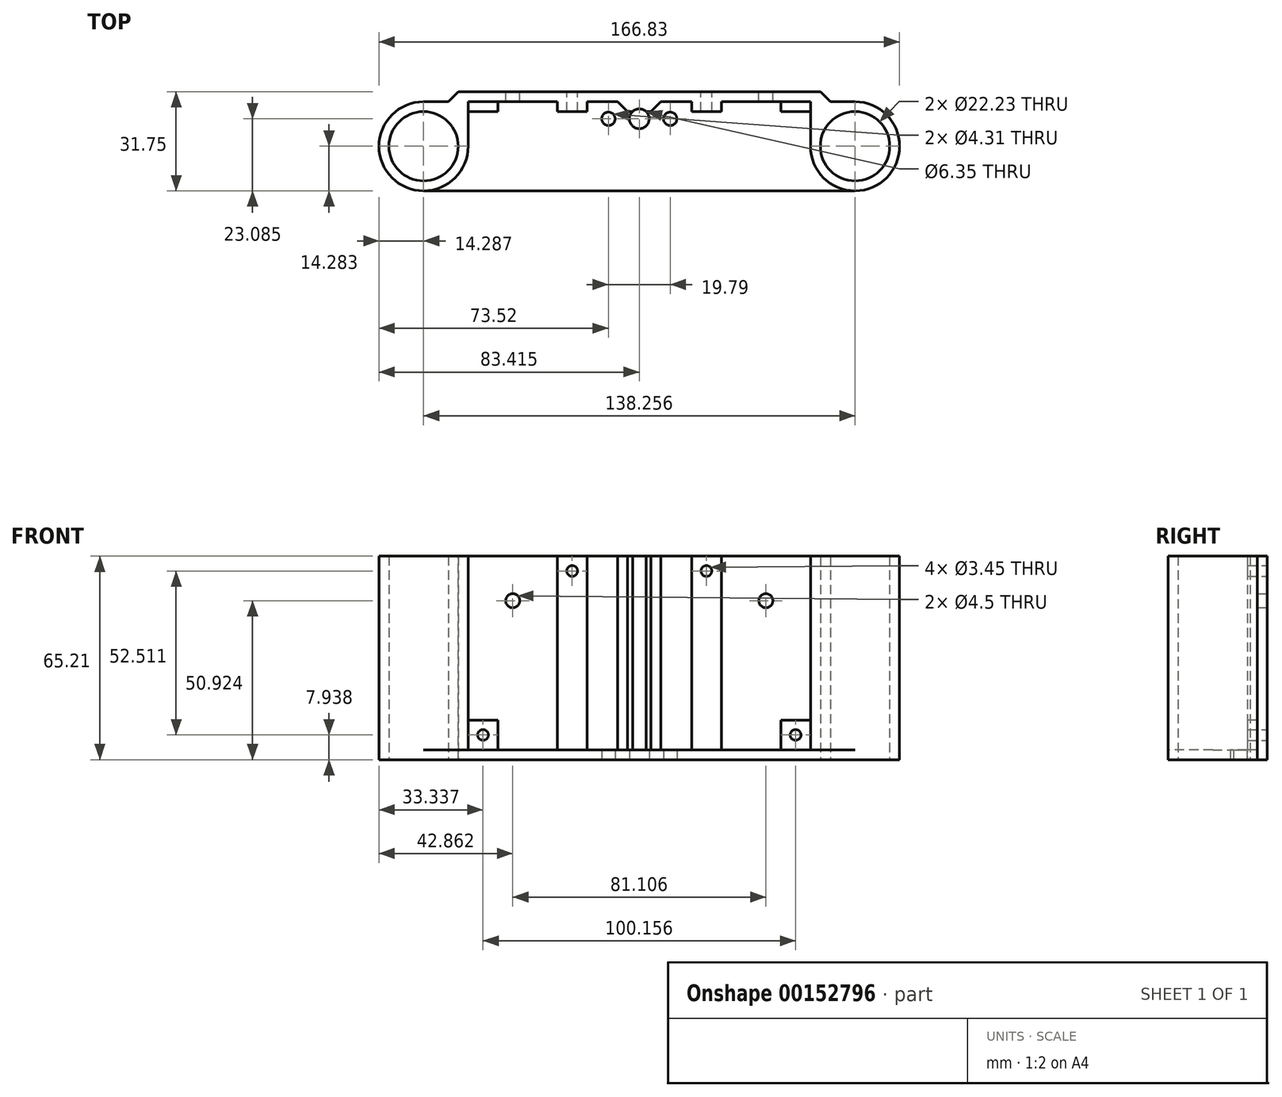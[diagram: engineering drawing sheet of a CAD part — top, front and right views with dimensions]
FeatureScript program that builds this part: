
annotation { "Feature Type Name" : "Feature", "Feature Type Description" : "" }
export const myFeature = defineFeature(function(context is Context, id is Id, definition is map)
    precondition{}
    {
        {
            var Q0;
            Q0=qCreatedBy(makeId("Top.planeOp"),FACE);
            var sketch = newSketch(context, id + "F0", { "sketchPlane" : qUnion([Q0])});
            skLineSegment(sketch, "E0.bottom", {"start": v(0, 0) * mm, "end": v(22.22, 0) * mm});
            skLineSegment(sketch, "E1.top", {"start": v(0, -14.29) * mm, "end": v(28.58, -14.29) * mm, "construction": true});
            skLineSegment(sketch, "E1.left", {"start": v(0, 0) * mm, "end": v(0, -14.29) * mm});
            skLineSegment(sketch, "E1.right", {"start": v(28.58, -3.18) * mm, "end": v(28.58, -14.29) * mm});
            skArc(sketch, "E2", {"start": v(0, -14.29) * mm, "mid": v(14.29, -28.57) * mm, "end": v(28.58, -14.29) * mm});
            skLineSegment(sketch, "E3", {"start": v(28.58, -3.18) * mm, "end": v(138.26, -3.18) * mm});
            skLineSegment(sketch, "E4.top", {"start": v(138.26, -14.29) * mm, "end": v(166.83, -14.29) * mm, "construction": true});
            skLineSegment(sketch, "E4.left", {"start": v(138.26, -3.18) * mm, "end": v(138.26, -14.29) * mm});
            skLineSegment(sketch, "E4.right", {"start": v(166.83, 0) * mm, "end": v(166.83, -14.29) * mm});
            skArc(sketch, "E5", {"start": v(138.26, -14.29) * mm, "mid": v(152.54, -28.57) * mm, "end": v(166.83, -14.29) * mm});
            skCircle(sketch, "E6", {"center": v(14.29, -14.29) * mm, "radius": 11.11 * mm});
            skCircle(sketch, "E7", {"center": v(152.54, -14.29) * mm, "radius": 11.11 * mm});
            skLineSegment(sketch, "E8", {"start": v(22.23, 0) * mm, "end": v(22.23, 3.18) * mm});
            skLineSegment(sketch, "E9", {"start": v(22.22, 3.17) * mm, "end": v(144.6, 3.17) * mm});
            skLineSegment(sketch, "E10", {"start": v(144.6, 3.18) * mm, "end": v(144.6, 0) * mm});
            skLineSegment(sketch, "E11", {"start": v(144.6, 0) * mm, "end": v(166.83, 0) * mm});
            skSolve(sketch);
        }
        {
            var Q0;
            Q0=qSketchRegion(id+"F0",true);
            extrude(context, id + "F1", {"entities" : qUnion([Q0]), "depth" : 65.2 * mm});
        }
        {
            var Q0;
            Q0=makeQuery(id+"F1.opExtrude","CAP_FACE",FACE,{"disambiguationData":[OSD([sQuery(id+"F0.wireOp",EDGE,"E0.bottom"),sQuery(id+"F0.wireOp",EDGE,"E0.top"),sQuery(id+"F0.wireOp",EDGE,"E0.left"),sQuery(id+"F0.wireOp",EDGE,"E1.left"),sQuery(id+"F0.wireOp",EDGE,"E1.right"),sQuery(id+"F0.wireOp",EDGE,"E2"),sQuery(id+"F0.wireOp",EDGE,"E3"),sQuery(id+"F0.wireOp",EDGE,"E4.left"),sQuery(id+"F0.wireOp",EDGE,"E4.right"),sQuery(id+"F0.wireOp",EDGE,"E5"),sQuery(id+"F0.wireOp",EDGE,"SdDxLh9R-VBPd-SPTP-oL8X-EhF4jRjkJOkv.bottom"),sQuery(id+"F0.wireOp",EDGE,"SdDxLh9R-VBPd-SPTP-oL8X-EhF4jRjkJOkv.right"),sQuery(id+"F0.wireOp",EDGE,"E6"),sQuery(id+"F0.wireOp",EDGE,"E7")])],"isStart":true});
            var sketch = newSketch(context, id + "F2", { "sketchPlane" : qUnion([Q0])});
            skLineSegment(sketch, "E12", {"start": v(14.29, 28.58) * mm, "end": v(152.54, 28.58) * mm});
            skLineSegment(sketch, "E13.top", {"start": v(28.58, 3.18) * mm, "end": v(138.26, 3.18) * mm});
            skLineSegment(sketch, "E13.left", {"start": v(28.58, 14.29) * mm, "end": v(28.58, 3.18) * mm});
            skLineSegment(sketch, "E13.right", {"start": v(138.26, 14.29) * mm, "end": v(138.26, 3.18) * mm});
            skArc(sketch, "E14", {"start": v(152.54, 28.57) * mm, "mid": v(142.44, 24.4) * mm, "end": v(138.26, 14.29) * mm});
            skArc(sketch, "E15", {"start": v(28.58, 14.29) * mm, "mid": v(24.4, 24.4) * mm, "end": v(14.29, 28.57) * mm});
            skSolve(sketch);
        }
        {
            var Q0;
            Q0=makeQuery(id+"F2.imprint","IMPRINT",FACE,{"disambiguationData":[TD([[makeQuery(id+"F2.imprint","IMPRINT",EDGE,{"derivedFrom":sQuery(id+"F2.wireOp",EDGE,"E12")}),-1.0]])]});
            var Q1;
            {var subQ0=sQuery(id+"F2.wireOp",EDGE,"YKqQdaZC-LU7M-u9Vu-8tjr-K4hHchLtnBJy");var subQ1=sQuery(id+"F2.wireOp",EDGE,"E13.top");var subQ2=makeQuery(id+"F2.imprint","INTERSECT",VERTEX,{"disambiguationData":[OD(0.0)],"derivedFrom":[subQ1,subQ0]});Q1=makeQuery(id+"F2.imprint","IMPRINT",FACE,{"disambiguationData":[TD([[makeQuery(id+"F2.imprint","IMPRINT",EDGE,{"disambiguationData":[TD([[subQ2,-1.0]])],"derivedFrom":subQ1}),-1.0]])]});}
            var Q2;
            Q2=makeQuery(id+"FjmdNtaRYLObFBn_1.boolean.opBoolean","COPY",FACE,{"derivedFrom":makeQuery(id+"FjmdNtaRYLObFBn_1.opExtrude","CAP_FACE",FACE,{"disambiguationData":[OSD([sQuery(id+"FSosjeWW6qpsHIW_1.wireOp",EDGE,"e9cDil25-53kW-lShf-zMKn-JTNJqIeN1P7c")])],"isStart":false})});
            extrude(context, id + "F3", {"entities" : qUnion([Q0, Q1]), "operationType" : NewBodyOperationType.ADD, "oppositeDirection" : true, "endBoundEntityFace" : qUnion([Q2]), "depth" : 3.17 * mm});
        }
        {
            var Q0;
            Q0=makeQuery(id+"F1.opExtrude","SWEPT_EDGE",EDGE,{"disambiguationData":[OSD([sQuery(id+"F0.wireOp",EDGE,"E0.bottom"),sQuery(id+"F0.wireOp",EDGE,"E1.left")])]});
            var Q1;
            Q1=makeQuery(id+"F1.opExtrude","SWEPT_EDGE",EDGE,{"disambiguationData":[OSD([sQuery(id+"F0.wireOp",EDGE,"E4.right"),sQuery(id+"F0.wireOp",EDGE,"E11")])]});
            var Q2;
            Q2=makeQuery(id+"F1.opExtrude","SWEPT_EDGE",EDGE,{"disambiguationData":[OSD([sQuery(id+"F0.wireOp",EDGE,"E0.bottom"),sQuery(id+"F0.wireOp",EDGE,"E1.left")])]});
            fillet(context, id + "F4", {"entities" : qUnion([Q0, Q1, Q2]), "radius" : 14.29 * mm, "tangentPropagation" : true, "allowEdgeOverflow" : false});
        }
        {
            var Q0;
            Q0=makeQuery(id+"F1.opExtrude","SWEPT_FACE",FACE,{"disambiguationData":[OSD([sQuery(id+"F0.wireOp",EDGE,"E9")])]});
            var sketch = newSketch(context, id + "F5", { "sketchPlane" : qUnion([Q0])});
            skLineSegment(sketch, "E16.bottom", {"start": v(-138.26, 65.21) * mm, "end": v(-123.97, 65.21) * mm, "construction": true});
            skLineSegment(sketch, "E16.top", {"start": v(-138.26, 50.92) * mm, "end": v(-123.97, 50.92) * mm, "construction": true});
            skLineSegment(sketch, "E16.left", {"start": v(-138.26, 65.21) * mm, "end": v(-138.26, 50.92) * mm, "construction": true});
            skLineSegment(sketch, "E16.right", {"start": v(-123.97, 65.21) * mm, "end": v(-123.97, 50.92) * mm, "construction": true});
            skLineSegment(sketch, "E17.bottom", {"start": v(-28.58, 65.21) * mm, "end": v(-42.86, 65.21) * mm, "construction": true});
            skLineSegment(sketch, "E17.top", {"start": v(-28.57, 50.92) * mm, "end": v(-42.86, 50.92) * mm, "construction": true});
            skLineSegment(sketch, "E17.left", {"start": v(-28.57, 65.21) * mm, "end": v(-28.57, 50.92) * mm, "construction": true});
            skLineSegment(sketch, "E17.right", {"start": v(-42.86, 65.21) * mm, "end": v(-42.86, 50.92) * mm, "construction": true});
            skLineSegment(sketch, "E18", {"start": v(-123.97, 60.45) * mm, "end": v(-104.92, 60.45) * mm, "construction": true});
            skLineSegment(sketch, "E19", {"start": v(-104.92, 60.45) * mm, "end": v(-61.91, 60.45) * mm, "construction": true});
            skLineSegment(sketch, "E20", {"start": v(-61.91, 60.45) * mm, "end": v(-42.86, 60.45) * mm, "construction": true});
            skLineSegment(sketch, "E21", {"start": v(-83.42, 60.45) * mm, "end": v(-83.42, 65.21) * mm, "construction": true});
            skLineSegment(sketch, "E22", {"start": v(-133.5, 3.17) * mm, "end": v(-133.5, 7.94) * mm, "construction": true});
            skLineSegment(sketch, "E23", {"start": v(-33.34, 3.17) * mm, "end": v(-33.34, 7.94) * mm, "construction": true});
            skCircle(sketch, "E24", {"center": v(-123.97, 50.92) * mm, "radius": 2.25 * mm});
            skCircle(sketch, "E25", {"center": v(-104.92, 60.45) * mm, "radius": 1.73 * mm});
            skCircle(sketch, "E26", {"center": v(-61.91, 60.45) * mm, "radius": 1.73 * mm});
            skCircle(sketch, "E27", {"center": v(-42.86, 50.92) * mm, "radius": 2.25 * mm});
            skCircle(sketch, "E28", {"center": v(-133.5, 7.94) * mm, "radius": 1.73 * mm});
            skCircle(sketch, "E29", {"center": v(-33.34, 7.94) * mm, "radius": 1.73 * mm});
            skLineSegment(sketch, "E30", {"start": v(-133.5, 7.94) * mm, "end": v(-138.26, 7.94) * mm, "construction": true});
            skLineSegment(sketch, "E31", {"start": v(-33.34, 7.94) * mm, "end": v(-28.58, 7.94) * mm, "construction": true});
            skSolve(sketch);
        }
        {
            var Q0;
            Q0 = qSketchRegion(id + "F5", true);
            var Q1;
            Q1=makeQuery(id+"F1.opExtrude","SWEPT_FACE",FACE,{"disambiguationData":[OSD([sQuery(id+"F0.wireOp",EDGE,"E3")])]});
            extrude(context, id + "F6", {"entities" : qUnion([Q0]), "operationType" : NewBodyOperationType.REMOVE, "endBound" : BoundingType.UP_TO_SURFACE, "oppositeDirection" : true, "endBoundEntityFace" : qUnion([Q1]), "depth" : 25.4 * mm});
        }
        {
            var Q0;
            {var subQ0=sQuery(id+"F0.wireOp",EDGE,"E11");var subQ1=sQuery(id+"F0.wireOp",EDGE,"E10");var subQ2=sQuery(id+"F0.wireOp",EDGE,"E9");var subQ3=sQuery(id+"F0.wireOp",EDGE,"E8");var subQ4=sQuery(id+"F0.wireOp",EDGE,"E7");var subQ5=sQuery(id+"F0.wireOp",EDGE,"E6");var subQ6=sQuery(id+"F0.wireOp",EDGE,"E5");var subQ7=sQuery(id+"F0.wireOp",EDGE,"E4.right");var subQ8=sQuery(id+"F0.wireOp",EDGE,"E2");var subQ9=sQuery(id+"F0.wireOp",EDGE,"E1.left");var subQ10=sQuery(id+"F0.wireOp",EDGE,"E0.bottom");Q0=makeQuery(id+"F3.boolean.opBoolean","MERGE",FACE,{"derivedFrom":[makeQuery(id+"F1.opExtrude","CAP_FACE",FACE,{"disambiguationData":[OSD([subQ10,subQ9,sQuery(id+"F0.wireOp",EDGE,"E1.right"),subQ8,sQuery(id+"F0.wireOp",EDGE,"E3"),sQuery(id+"F0.wireOp",EDGE,"E4.left"),subQ7,subQ6,subQ5,subQ4,subQ3,subQ2,subQ1,subQ0])],"isStart":true}),makeQuery(id+"F3.opExtrude","CAP_FACE",FACE,{"disambiguationData":[OSD([subQ10,subQ9,subQ8,subQ7,subQ6,subQ5,subQ4,subQ3,subQ2,subQ1,subQ0,sQuery(id+"F2.wireOp",EDGE,"E12")])],"isStart":true})]});}
            var sketch = newSketch(context, id + "F7", { "sketchPlane" : qUnion([Q0])});
            skLineSegment(sketch, "E32", {"start": v(14.29, 14.29) * mm, "end": v(152.54, 14.29) * mm, "construction": true});
            skLineSegment(sketch, "E33", {"start": v(83.42, 14.29) * mm, "end": v(83.42, 5.48) * mm, "construction": true});
            skCircle(sketch, "E34", {"center": v(83.42, 5.48) * mm, "radius": 3.18 * mm});
            skLineSegment(sketch, "E35", {"start": v(73.52, 5.48) * mm, "end": v(93.31, 5.48) * mm, "construction": true});
            skCircle(sketch, "E36", {"center": v(73.52, 5.48) * mm, "radius": 2.15 * mm});
            skCircle(sketch, "E37", {"center": v(93.31, 5.48) * mm, "radius": 2.15 * mm});
            skCircle(sketch, "E38.cCircle", {"center": v(83.42, 5.48) * mm, "radius": 4.45 * mm, "construction": true});
            skLineSegment(sketch, "E38.0", {"start": v(85.98, 9.93) * mm, "end": v(88.55, 5.48) * mm, "construction": true});
            skLineSegment(sketch, "E38.1", {"start": v(88.55, 5.48) * mm, "end": v(85.98, 1.04) * mm, "construction": true});
            skLineSegment(sketch, "E38.2", {"start": v(85.98, 1.04) * mm, "end": v(80.85, 1.04) * mm, "construction": true});
            skLineSegment(sketch, "E38.3", {"start": v(80.85, 1.04) * mm, "end": v(78.28, 5.48) * mm, "construction": true});
            skLineSegment(sketch, "E38.4", {"start": v(78.28, 5.48) * mm, "end": v(80.85, 9.93) * mm, "construction": true});
            skLineSegment(sketch, "E38.5", {"start": v(80.85, 9.93) * mm, "end": v(85.98, 9.93) * mm, "construction": true});
            skPoint(sketch, "E38.0.midPoint", {"position": v(87.26, 7.7) * mm});
            skSolve(sketch);
        }
        {
            var Q0;
            Q0 = qSketchRegion(id + "F7", true);
            var Q1;
            Q1=makeQuery(id+"F1.opExtrude","CAP_FACE",FACE,{"disambiguationData":[OSD([sQuery(id+"F0.wireOp",EDGE,"E0.bottom"),sQuery(id+"F0.wireOp",EDGE,"E1.left"),sQuery(id+"F0.wireOp",EDGE,"E1.right"),sQuery(id+"F0.wireOp",EDGE,"E2"),sQuery(id+"F0.wireOp",EDGE,"E3"),sQuery(id+"F0.wireOp",EDGE,"E4.left"),sQuery(id+"F0.wireOp",EDGE,"E4.right"),sQuery(id+"F0.wireOp",EDGE,"E5"),sQuery(id+"F0.wireOp",EDGE,"E6"),sQuery(id+"F0.wireOp",EDGE,"E7"),sQuery(id+"F0.wireOp",EDGE,"E8"),sQuery(id+"F0.wireOp",EDGE,"E9"),sQuery(id+"F0.wireOp",EDGE,"E10"),sQuery(id+"F0.wireOp",EDGE,"E11")])],"isStart":false});
            extrude(context, id + "F8", {"entities" : qUnion([Q0]), "operationType" : NewBodyOperationType.REMOVE, "endBound" : BoundingType.UP_TO_SURFACE, "oppositeDirection" : true, "endBoundEntityFace" : qUnion([Q1]), "depth" : 25.4 * mm});
        }
        {
            var Q0;
            Q0=makeQuery(id+"F1.opExtrude","SWEPT_FACE",FACE,{"disambiguationData":[OSD([sQuery(id+"F0.wireOp",EDGE,"E3")])]});
            var sketch = newSketch(context, id + "F9", { "sketchPlane" : qUnion([Q0])});
            skLineSegment(sketch, "E39.left", {"start": v(28.58, 65.21) * mm, "end": v(28.58, 12.7) * mm});
            skLineSegment(sketch, "E39.right", {"start": v(138.26, 65.21) * mm, "end": v(138.26, 12.7) * mm});
            skLineSegment(sketch, "E40.bottom", {"start": v(57.15, 65.21) * mm, "end": v(66.67, 65.21) * mm, "construction": true});
            skLineSegment(sketch, "E40.top", {"start": v(57.15, 3.17) * mm, "end": v(66.68, 3.17) * mm, "construction": true});
            skLineSegment(sketch, "E40.left", {"start": v(57.15, 65.21) * mm, "end": v(57.15, 3.17) * mm});
            skLineSegment(sketch, "E40.right", {"start": v(66.67, 65.21) * mm, "end": v(66.67, 3.18) * mm});
            skLineSegment(sketch, "E41.bottom", {"start": v(100.16, 65.21) * mm, "end": v(109.68, 65.21) * mm, "construction": true});
            skLineSegment(sketch, "E41.top", {"start": v(100.16, 3.17) * mm, "end": v(109.68, 3.17) * mm, "construction": true});
            skLineSegment(sketch, "E41.left", {"start": v(100.16, 65.21) * mm, "end": v(100.16, 3.17) * mm});
            skLineSegment(sketch, "E41.right", {"start": v(109.68, 65.21) * mm, "end": v(109.68, 3.17) * mm});
            skLineSegment(sketch, "E42", {"start": v(61.91, 65.21) * mm, "end": v(61.91, 60.45) * mm, "construction": true});
            skLineSegment(sketch, "E43", {"start": v(61.91, 60.45) * mm, "end": v(66.67, 60.45) * mm, "construction": true});
            skLineSegment(sketch, "E44", {"start": v(104.92, 60.45) * mm, "end": v(104.92, 65.21) * mm, "construction": true});
            skLineSegment(sketch, "E45.bottom", {"start": v(138.26, 3.18) * mm, "end": v(128.73, 3.18) * mm, "construction": true});
            skLineSegment(sketch, "E45.top", {"start": v(138.26, 12.7) * mm, "end": v(128.73, 12.7) * mm});
            skLineSegment(sketch, "E45.left", {"start": v(138.26, 3.18) * mm, "end": v(138.26, 12.7) * mm, "construction": true});
            skLineSegment(sketch, "E45.right", {"start": v(128.73, 3.18) * mm, "end": v(128.73, 12.7) * mm});
            skPoint(sketch, "E45.middle", {"position": v(133.5, 7.94) * mm});
            skLineSegment(sketch, "E46.bottom", {"start": v(28.58, 3.18) * mm, "end": v(38.1, 3.18) * mm, "construction": true});
            skLineSegment(sketch, "E46.top", {"start": v(28.58, 12.7) * mm, "end": v(38.1, 12.7) * mm});
            skLineSegment(sketch, "E46.left", {"start": v(28.58, 3.18) * mm, "end": v(28.58, 12.7) * mm, "construction": true});
            skLineSegment(sketch, "E46.right", {"start": v(38.1, 3.18) * mm, "end": v(38.1, 12.7) * mm});
            skPoint(sketch, "E46.middle", {"position": v(33.34, 7.94) * mm});
            skLineSegment(sketch, "E47", {"start": v(38.1, 3.18) * mm, "end": v(57.15, 3.17) * mm});
            skLineSegment(sketch, "E48", {"start": v(128.73, 3.18) * mm, "end": v(109.68, 3.17) * mm});
            skLineSegment(sketch, "E49", {"start": v(109.68, 65.21) * mm, "end": v(138.26, 65.21) * mm});
            skLineSegment(sketch, "E50", {"start": v(57.15, 65.21) * mm, "end": v(28.58, 65.21) * mm});
            skLineSegment(sketch, "E51.bottom", {"start": v(85.6, 65.21) * mm, "end": v(87.18, 65.21) * mm, "construction": true});
            skLineSegment(sketch, "E51.top", {"start": v(85.6, 3.17) * mm, "end": v(87.18, 3.17) * mm, "construction": true});
            skLineSegment(sketch, "E51.left", {"start": v(85.6, 65.21) * mm, "end": v(85.6, 3.17) * mm, "construction": true});
            skLineSegment(sketch, "E51.right", {"start": v(87.18, 65.21) * mm, "end": v(87.18, 3.17) * mm});
            skLineSegment(sketch, "E52.bottom", {"start": v(81.24, 65.21) * mm, "end": v(79.65, 65.21) * mm, "construction": true});
            skLineSegment(sketch, "E52.top", {"start": v(81.24, 3.17) * mm, "end": v(79.65, 3.17) * mm, "construction": true});
            skLineSegment(sketch, "E52.left", {"start": v(81.24, 65.21) * mm, "end": v(81.24, 3.17) * mm, "construction": true});
            skLineSegment(sketch, "E52.right", {"start": v(79.65, 65.21) * mm, "end": v(79.65, 3.17) * mm});
            skLineSegment(sketch, "E53", {"start": v(66.67, 65.21) * mm, "end": v(79.65, 65.21) * mm});
            skLineSegment(sketch, "E54", {"start": v(87.18, 65.21) * mm, "end": v(100.16, 65.21) * mm});
            skLineSegment(sketch, "E55", {"start": v(100.16, 3.17) * mm, "end": v(87.18, 3.17) * mm});
            skLineSegment(sketch, "E56", {"start": v(79.65, 3.17) * mm, "end": v(66.68, 3.17) * mm});
            skSolve(sketch);
        }
        {
            var Q0;
            Q0 = qSketchRegion(id + "F9", true);
            extrude(context, id + "F10", {"entities" : qUnion([Q0]), "operationType" : NewBodyOperationType.REMOVE, "oppositeDirection" : true, "depth" : 3.17 * mm});
        }
        {
            var Q0;
            Q0=makeQuery(id+"F1.opExtrude","SWEPT_EDGE",EDGE,{"disambiguationData":[OSD([sQuery(id+"F0.wireOp",EDGE,"E8"),sQuery(id+"F0.wireOp",EDGE,"E9")])]});
            var Q1;
            Q1=makeQuery(id+"F1.opExtrude","SWEPT_EDGE",EDGE,{"disambiguationData":[OSD([sQuery(id+"F0.wireOp",EDGE,"E9"),sQuery(id+"F0.wireOp",EDGE,"E10")])]});
            var Q2;
            Q2=makeQuery(id+"F10.boolean.opBoolean","COPY",EDGE,{"derivedFrom":makeQuery(id+"F10.opExtrude","CAP_EDGE",EDGE,{"disambiguationData":[OSD([sQuery(id+"F9.wireOp",EDGE,"E51.right")])],"isStart":false})});
            var Q3;
            Q3=makeQuery(id+"F10.boolean.opBoolean","COPY",EDGE,{"derivedFrom":makeQuery(id+"F10.opExtrude","CAP_EDGE",EDGE,{"disambiguationData":[OSD([sQuery(id+"F9.wireOp",EDGE,"E52.right")])],"isStart":false})});
            chamfer(context, id + "F11", {"entities" : qUnion([Q0, Q1, Q2, Q3]), "width" : 3.17 * mm, "tangentPropagation" : true});
        }
    });
